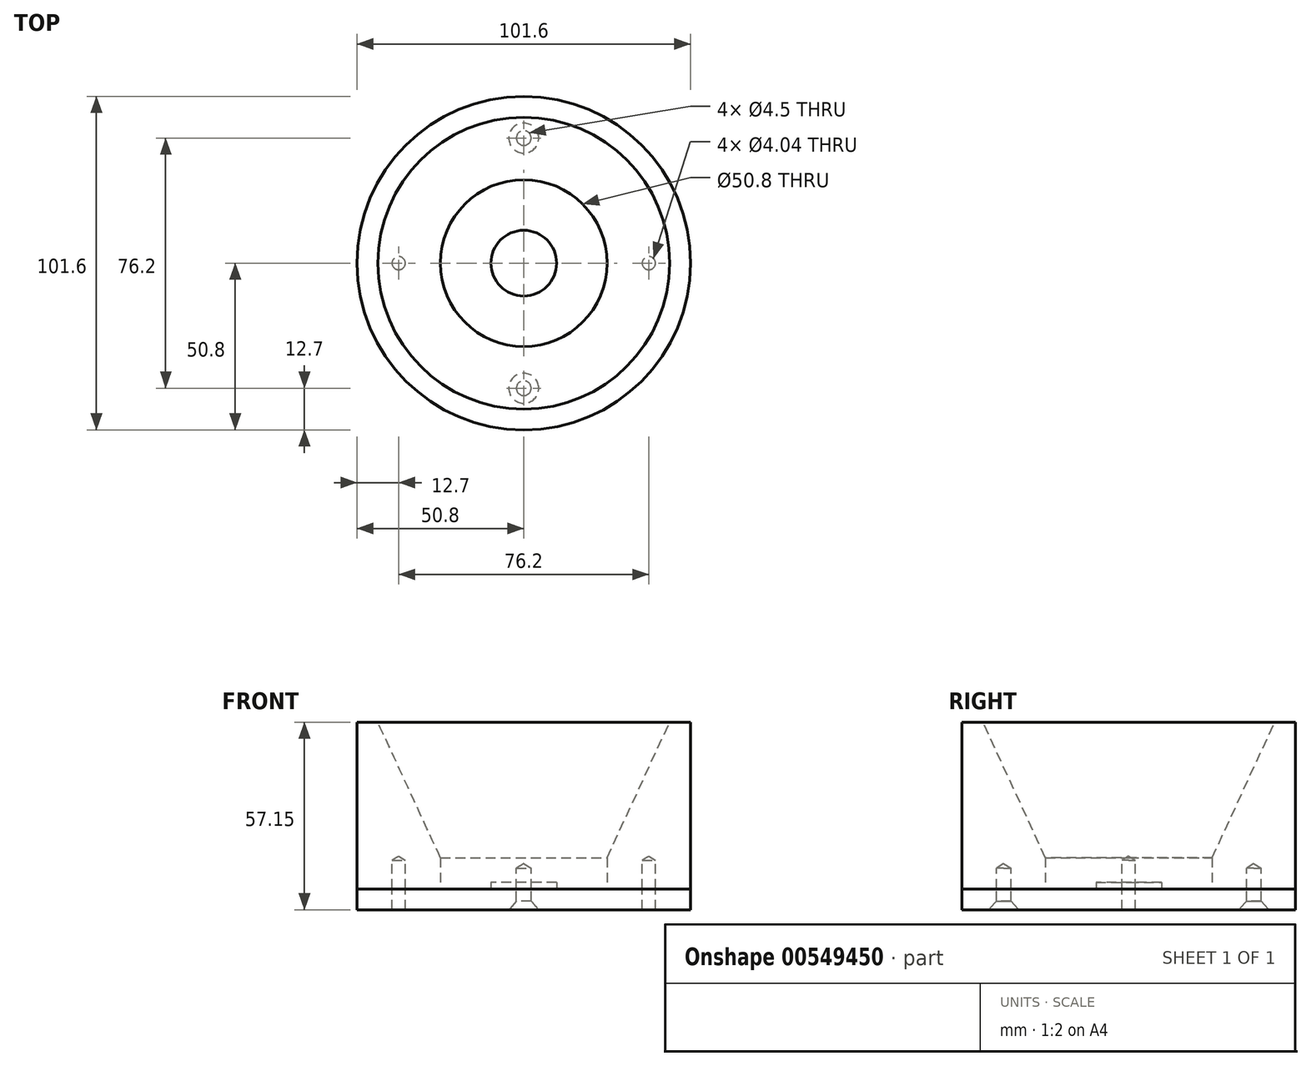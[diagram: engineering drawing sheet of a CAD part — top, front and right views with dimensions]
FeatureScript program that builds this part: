
annotation { "Feature Type Name" : "Feature", "Feature Type Description" : "" }
export const myFeature = defineFeature(function(context is Context, id is Id, definition is map)
    precondition{}
    {
        {
            var Q0;
            Q0=qCreatedBy(makeId("Top.planeOp"),FACE);
            var sketch = newSketch(context, id + "F0", { "sketchPlane" : qUnion([Q0])});
            skCircle(sketch, "E0", {"center": v(0, 0) * mm, "radius": 25.4 * mm});
            skSolve(sketch);
        }
        {
            var Q0;
            Q0=makeQuery(id+"F0.imprint","IMPRINT",FACE,{"disambiguationData":[TD([[makeQuery(id+"F0.imprint","IMPRINT",EDGE,{"derivedFrom":sQuery(id+"F0.wireOp",EDGE,"E0")}),1.0]])]});
            extrude(context, id + "F1", {"entities" : qUnion([Q0]), "depth" : 3 / 203.2 * mm, "offsetDistance" : 25.4 * mm});
        }
        {
            var Q0;
            Q0=makeQuery(id+"F1.opExtrude","CAP_FACE",FACE,{"disambiguationData":[OSD([sQuery(id+"F0.wireOp",EDGE,"E0")])],"isStart":false});
            var sketch = newSketch(context, id + "F2", { "sketchPlane" : qUnion([Q0])});
            skCircle(sketch, "E1", {"center": v(0, 0) * mm, "radius": 10 * mm});
            skSolve(sketch);
        }
        {
            var Q0;
            Q0=makeQuery(id+"F2.imprint","IMPRINT",FACE,{"disambiguationData":[TD([[makeQuery(id+"F2.imprint","IMPRINT",EDGE,{"derivedFrom":sQuery(id+"F2.wireOp",EDGE,"E1")}),1.0]])]});
            extrude(context, id + "F3", {"entities" : qUnion([Q0]), "depth" : 2 * mm, "offsetDistance" : 25.4 * mm});
        }
        {
            var Q0;
            Q0=qCreatedBy(makeId("Top.planeOp"),FACE);
            var sketch = newSketch(context, id + "F4", { "sketchPlane" : qUnion([Q0])});
            skCircle(sketch, "E2", {"center": v(0, 0) * mm, "radius": 50.8 * mm});
            skSolve(sketch);
        }
        {
            var Q0;
            Q0=qCreatedBy(makeId("Right.planeOp"),FACE);
            var sketch = newSketch(context, id + "F5", { "sketchPlane" : qUnion([Q0])});
            skLineSegment(sketch, "E3", {"start": v(0, 0) * mm, "end": v(-50.8, 0) * mm});
            skLineSegment(sketch, "E4", {"start": v(-50.8, 0) * mm, "end": v(-50.8, 50.8) * mm});
            skLineSegment(sketch, "E5", {"start": v(-50.8, 50.8) * mm, "end": v(-44.45, 50.8) * mm});
            skLineSegment(sketch, "E6.0", {"start": v(-25.4, 9.53) * mm, "end": v(25.4, 9.53) * mm});
            skLineSegment(sketch, "E7", {"start": v(-44.45, 50.8) * mm, "end": v(-25.4, 9.53) * mm});
            skLineSegment(sketch, "E8", {"start": v(-25.4, 9.53) * mm, "end": v(-25.4, 0) * mm});
            skLineSegment(sketch, "E9", {"start": v(0, 0) * mm, "end": v(0, 70.3) * mm, "construction": true});
            skSolve(sketch);
        }
        {
            var Q0;
            {var subQ0=sQuery(id+"F5.wireOp",EDGE,"E4");Q0=makeQuery(id+"F5.imprint","IMPRINT",FACE,{"disambiguationData":[TD([[makeQuery(id+"F5.imprint","IMPRINT",EDGE,{"derivedFrom":subQ0}),-1.0]])]});}
            var Q1;
            Q1=sQuery(id+"F5.wireOp",EDGE,"E9");
            revolve(context, id + "F6", {"surfaceOperationType" : NewSurfaceOperationType.NEW, "entities" : qUnion([Q0]), "axis" : qUnion([Q1]), "revolveType" : RevolveType.FULL});
        }
        {
            var Q0;
            Q0=makeQuery(id+"F4.imprint","IMPRINT",FACE,{"disambiguationData":[TD([[makeQuery(id+"F4.imprint","IMPRINT",EDGE,{"derivedFrom":sQuery(id+"F4.wireOp",EDGE,"E2")}),1.0]])]});
            var sketch = newSketch(context, id + "F7", { "sketchPlane" : qUnion([Q0])});
            skPoint(sketch, "E10.0", {"position": v(0, 0) * mm});
            skCircle(sketch, "E11.0", {"center": v(0, 0) * mm, "radius": 50.8 * mm});
            skSolve(sketch);
        }
        {
            var Q0;
            Q0 = qSketchRegion(id + "F7", true);
            extrude(context, id + "F8", {"entities" : qUnion([Q0]), "oppositeDirection" : true, "depth" : 6.35 * mm, "offsetDistance" : 25.4 * mm});
        }
        {
            var Q0;
            Q0=makeQuery(id+"F8.opExtrude","CAP_FACE",FACE,{"disambiguationData":[OSD([sQuery(id+"F7.wireOp",EDGE,"E11.0")])],"isStart":false});
            var sketch = newSketch(context, id + "F9", { "sketchPlane" : qUnion([Q0])});
            skCircle(sketch, "E12.0", {"center": v(0, 0) * mm, "radius": 25.4 * mm});
            skCircle(sketch, "E13.0", {"center": v(0, 0) * mm, "radius": 50.8 * mm});
            skPoint(sketch, "E14", {"position": v(0, 12.7) * mm});
            skPoint(sketch, "E15", {"position": v(0, 38.1) * mm});
            skPoint(sketch, "E16.MirrorP", {"position": v(0, -12.7) * mm});
            skPoint(sketch, "E17.MirrorP", {"position": v(0, -38.1) * mm});
            skPoint(sketch, "E18", {"position": v(38.1, 0) * mm});
            skPoint(sketch, "E19.MirrorP", {"position": v(-38.1, 0) * mm});
            skSolve(sketch);
        }
        {
            var Q0;
            Q0=sQuery(id+"F9.wireOp",VERTEX,"E15");
            var Q1;
            Q1=sQuery(id+"F9.wireOp",VERTEX,"E14");
            var Q2;
            Q2=sQuery(id+"F9.wireOp",VERTEX,"E16.MirrorP");
            var Q3;
            Q3=sQuery(id+"F9.wireOp",VERTEX,"E17.MirrorP");
            var Q4;
            Q4=makeQuery(id+"F6.opRevolve","SWEPT_BODY",BODY,{"disambiguationData":[OSD([sQuery(id+"F5.wireOp",EDGE,"E3"),sQuery(id+"F5.wireOp",EDGE,"E4"),sQuery(id+"F5.wireOp",EDGE,"E5"),sQuery(id+"F5.wireOp",EDGE,"E7"),sQuery(id+"F5.wireOp",EDGE,"E8")])]});
            var Q5;
            Q5=makeQuery(id+"F8.opExtrude","SWEPT_BODY",BODY,{"disambiguationData":[OSD([sQuery(id+"F7.wireOp",EDGE,"E11.0")])]});
            var Q6;
            Q6=makeQuery(id+"F1.opExtrude","SWEPT_BODY",BODY,{"disambiguationData":[OSD([sQuery(id+"F0.wireOp",EDGE,"E0")])]});
            hole(context, id + "F10", {"style" : HoleStyle.C_SINK, "endStyle" : HoleEndStyle.BLIND, "standardTappedOrClearance" : lookupTablePath({ "standard" : "ANSI", "fit" : "Normal (ASME)", "size" : "#8", "type" : "Clearance" }), "standardBlindInLast" : lookupTablePath({ "fit" : "Free", "standard" : "ANSI", "size" : "#8", "type" : "Clearance" }), "holeDiameter" : 4.5 * mm, "cSinkDiameter" : 9.12 * mm, "cSinkAngle" : 82 * degree, "majorDiameter" : 6.35 * mm, "holeDepth" : 12.7 * mm, "tappedDepth" : 12.7 * mm, "tapClearance" : 3, "locations" : qUnion([Q0, Q1, Q2, Q3]), "scope" : qUnion([Q4, Q5, Q6])});
        }
        {
            var Q0;
            Q0=sQuery(id+"F9.wireOp",VERTEX,"E18");
            var Q1;
            Q1=sQuery(id+"F9.wireOp",VERTEX,"E19.MirrorP");
            var Q2;
            Q2=makeQuery(id+"F6.opRevolve","SWEPT_BODY",BODY,{"disambiguationData":[OSD([sQuery(id+"F5.wireOp",EDGE,"E3"),sQuery(id+"F5.wireOp",EDGE,"E4"),sQuery(id+"F5.wireOp",EDGE,"E5"),sQuery(id+"F5.wireOp",EDGE,"E7"),sQuery(id+"F5.wireOp",EDGE,"E8")])]});
            var Q3;
            Q3=makeQuery(id+"F8.opExtrude","SWEPT_BODY",BODY,{"disambiguationData":[OSD([sQuery(id+"F7.wireOp",EDGE,"E11.0")])]});
            hole(context, id + "F11", {"style" : HoleStyle.SIMPLE, "endStyle" : HoleEndStyle.BLIND, "standardTappedOrClearance" : lookupTablePath({ "standard" : "ANSI", "engagement" : "75%", "pitch" : "32 tpi", "size" : "#10", "type" : "Tapped" }), "standardBlindInLast" : lookupTablePath({ "standard" : "ANSI", "engagement" : "75%", "pitch" : "32 tpi", "size" : "#10", "type" : "Tapped" }), "holeDiameter" : 4.04 * mm, "majorDiameter" : 4.83 * mm, "showTappedDepth" : true, "holeDepth" : 15.08 * mm, "tappedDepth" : 12.7 * mm, "tapClearance" : 3, "locations" : qUnion([Q0, Q1]), "scope" : qUnion([Q2, Q3])});
        }
    });
